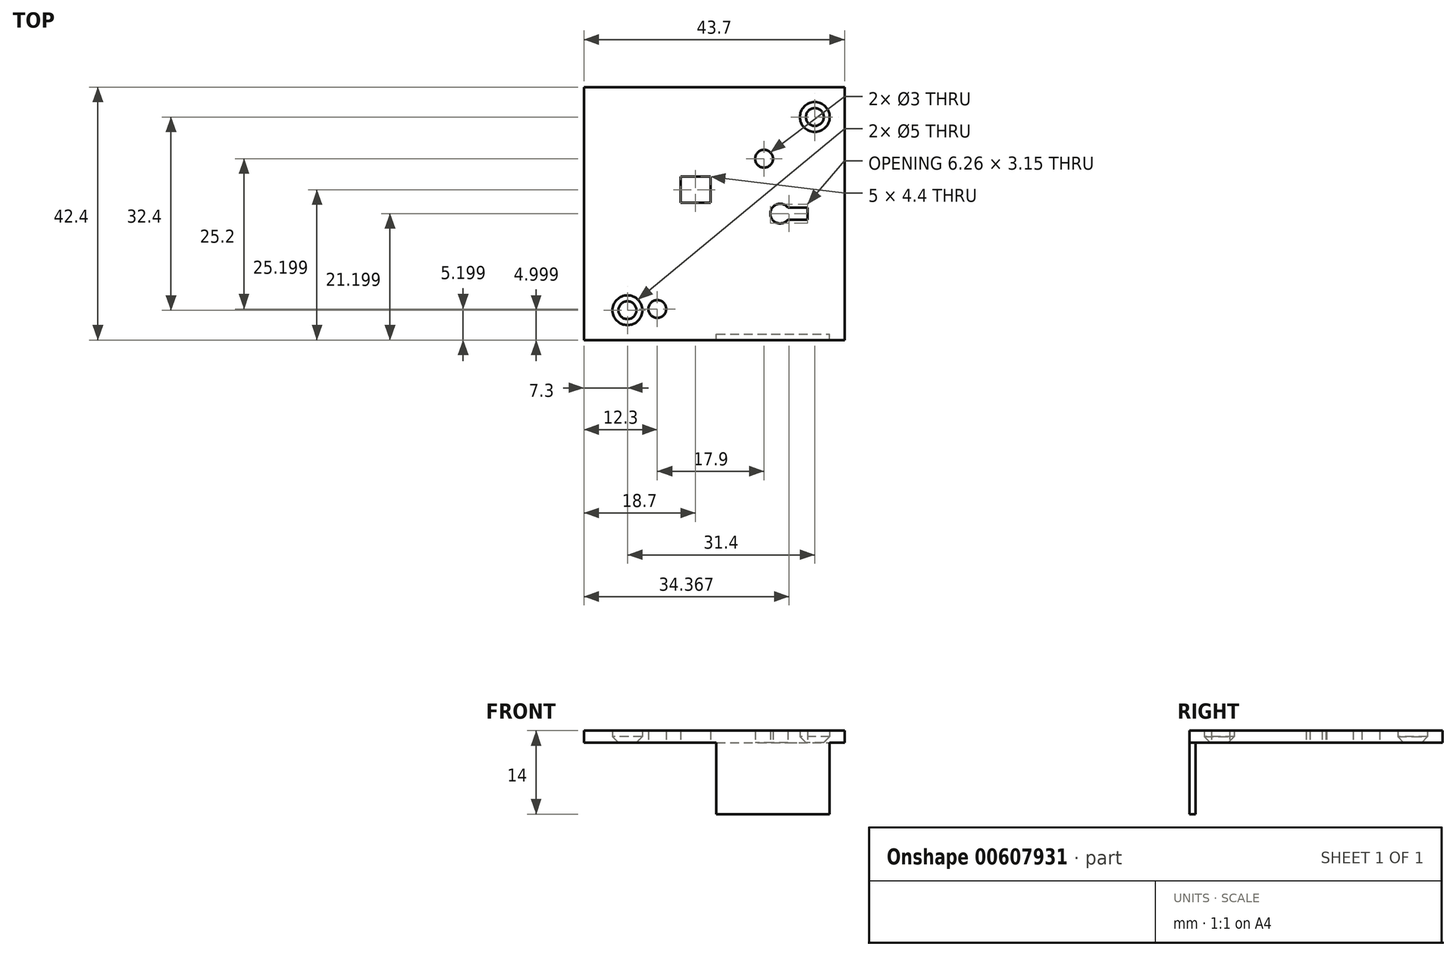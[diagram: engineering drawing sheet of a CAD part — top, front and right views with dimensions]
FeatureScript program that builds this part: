
annotation { "Feature Type Name" : "Feature", "Feature Type Description" : "" }
export const myFeature = defineFeature(function(context is Context, id is Id, definition is map)
    precondition{}
    {
        {
            var Q0;
            Q0=qCreatedBy(makeId("Top.planeOp"),FACE);
            var sketch = newSketch(context, id + "F0", { "sketchPlane" : qUnion([Q0])});
            skLineSegment(sketch, "E0.bottom", {"start": v(-16.91, 7.92) * mm, "end": v(-60.61, 7.92) * mm});
            skLineSegment(sketch, "E0.top", {"start": v(-16.91, 50.32) * mm, "end": v(-60.61, 50.32) * mm});
            skLineSegment(sketch, "E0.left", {"start": v(-16.91, 7.92) * mm, "end": v(-16.91, 50.32) * mm});
            skLineSegment(sketch, "E0.right", {"start": v(-60.61, 7.92) * mm, "end": v(-60.61, 50.32) * mm});
            skPoint(sketch, "E0.middle", {"position": v(-38.76, 29.12) * mm});
            skSolve(sketch);
        }
        {
            var Q0;
            Q0=makeQuery(id+"F0.imprint","IMPRINT",FACE,{"disambiguationData":[TD([[makeQuery(id+"F0.imprint","IMPRINT",EDGE,{"derivedFrom":sQuery(id+"F0.wireOp",EDGE,"E0.bottom")}),-1.0]])]});
            var sketch = newSketch(context, id + "F1", { "sketchPlane" : qUnion([Q0])});
            skCircle(sketch, "E1", {"center": v(-21.91, 45.32) * mm, "radius": 1.5 * mm});
            skCircle(sketch, "E2", {"center": v(-30.41, 38.32) * mm, "radius": 1.5 * mm});
            skCircle(sketch, "E3", {"center": v(-48.31, 13.12) * mm, "radius": 1.5 * mm});
            skLineSegment(sketch, "E4.bottom", {"start": v(-39.41, 30.92) * mm, "end": v(-44.41, 30.92) * mm});
            skLineSegment(sketch, "E4.top", {"start": v(-39.41, 35.32) * mm, "end": v(-44.41, 35.32) * mm});
            skLineSegment(sketch, "E4.left", {"start": v(-39.41, 30.92) * mm, "end": v(-39.41, 35.32) * mm});
            skLineSegment(sketch, "E4.right", {"start": v(-44.41, 30.92) * mm, "end": v(-44.41, 35.32) * mm});
            skPoint(sketch, "E4.middle", {"position": v(-41.91, 33.12) * mm});
            skCircle(sketch, "E5", {"center": v(-53.31, 12.92) * mm, "radius": 1.5 * mm});
            skCircle(sketch, "E6", {"center": v(-27.72, 29.12) * mm, "radius": 1.65 * mm});
            skLineSegment(sketch, "E7.bottom", {"start": v(-26.41, 30.12) * mm, "end": v(-23.11, 30.12) * mm});
            skLineSegment(sketch, "E7.top", {"start": v(-26.41, 28.12) * mm, "end": v(-23.11, 28.12) * mm});
            skLineSegment(sketch, "E7.left", {"start": v(-26.41, 30.12) * mm, "end": v(-26.41, 28.12) * mm});
            skLineSegment(sketch, "E7.right", {"start": v(-23.11, 30.12) * mm, "end": v(-23.11, 28.12) * mm});
            skSolve(sketch);
        }
        {
            var Q0;
            Q0=makeQuery(id+"F1.imprint","IMPRINT",FACE,{"disambiguationData":[TD([[makeQuery(id+"F1.imprint","IMPRINT",EDGE,{"derivedFrom":sQuery(id+"F1.wireOp",EDGE,"E1")}),-1.0]])]});
            extrude(context, id + "F2", {"entities" : qUnion([Q0]), "depth" : 1 * mm, "offsetDistance" : 25 * mm});
        }
        {
            var Q0;
            Q0=makeQuery(id+"F2.opExtrude","CAP_EDGE",EDGE,{"disambiguationData":[OSD([sQuery(id+"F1.wireOp",EDGE,"E1")])],"isStart":false});
            var Q1;
            Q1=makeQuery(id+"F2.opExtrude","CAP_EDGE",EDGE,{"disambiguationData":[OSD([sQuery(id+"F1.wireOp",EDGE,"E5")])],"isStart":false});
            chamfer(context, id + "F3", {"entities" : qUnion([Q0, Q1]), "width" : 1 * mm, "tangentPropagation" : true});
        }
        {
            var Q0;
            Q0=makeQuery(id+"F2.opExtrude","CAP_FACE",FACE,{"disambiguationData":[OSD([sQuery(id+"F0.wireOp",EDGE,"E0.bottom"),sQuery(id+"F0.wireOp",EDGE,"E0.top"),sQuery(id+"F0.wireOp",EDGE,"E0.left"),sQuery(id+"F0.wireOp",EDGE,"E0.right"),sQuery(id+"F1.wireOp",EDGE,"E1"),sQuery(id+"F1.wireOp",EDGE,"E2"),sQuery(id+"F1.wireOp",EDGE,"E3"),sQuery(id+"F1.wireOp",EDGE,"E4.bottom"),sQuery(id+"F1.wireOp",EDGE,"E4.top"),sQuery(id+"F1.wireOp",EDGE,"E4.left"),sQuery(id+"F1.wireOp",EDGE,"E4.right"),sQuery(id+"F1.wireOp",EDGE,"E5")])],"isStart":false});
            extrude(context, id + "F4", {"entities" : qUnion([Q0]), "operationType" : NewBodyOperationType.ADD, "depth" : 1 * mm, "offsetDistance" : 25 * mm});
        }
        {
            var Q0;
            Q0=makeQuery(id+"F0.imprint","IMPRINT",FACE,{"disambiguationData":[TD([[makeQuery(id+"F0.imprint","IMPRINT",EDGE,{"derivedFrom":sQuery(id+"F0.wireOp",EDGE,"E0.bottom")}),-1.0]])]});
            var sketch = newSketch(context, id + "F5", { "sketchPlane" : qUnion([Q0])});
            skLineSegment(sketch, "E8.bottom", {"start": v(-38.41, 7.92) * mm, "end": v(-19.41, 7.92) * mm});
            skLineSegment(sketch, "E8.top", {"start": v(-38.41, 8.92) * mm, "end": v(-19.41, 8.92) * mm});
            skLineSegment(sketch, "E8.left", {"start": v(-38.41, 7.92) * mm, "end": v(-38.41, 8.92) * mm});
            skLineSegment(sketch, "E8.right", {"start": v(-19.41, 7.92) * mm, "end": v(-19.41, 8.92) * mm});
            skSolve(sketch);
        }
        {
            var Q0;
            Q0 = qSketchRegion(id + "F5", true);
            extrude(context, id + "F6", {"entities" : qUnion([Q0]), "operationType" : NewBodyOperationType.ADD, "oppositeDirection" : true, "depth" : 12 * mm, "offsetDistance" : 25 * mm});
        }
    });
